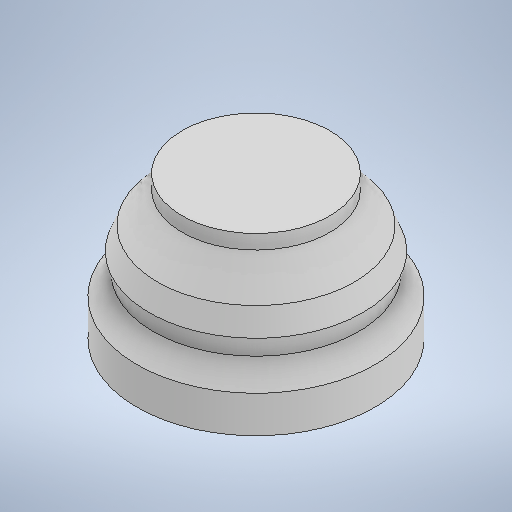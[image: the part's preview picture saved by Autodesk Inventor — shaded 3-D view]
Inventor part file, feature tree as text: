
AUTODESK INVENTOR PART (.ipt)
format: ipt  version: 2025.1 (Build 291241000, 241)  size: 297,984 bytes
history: native  units: mm
features: other x2, revolve x1, sketch x1
ambient origin geometry x8: Origin, YZ Plane, XZ Plane, XY Plane, X Axis, Y Axis, Z Axis, Center Point
bodies: Body1 (feature_tree)
feature tree (4):
  other  "Sólido1"
  revolve  "Revolución1"  [1 undecoded]
  sketch  "Boceto2"  dims[d16=90.0deg d18=12.0mm]
  other  "Imagen2"
note: 1 required parameter value undecoded (feature->parameter linkage not recoverable at this tier; creation-order binding heuristic only, values carry confidence <= 0.55)
